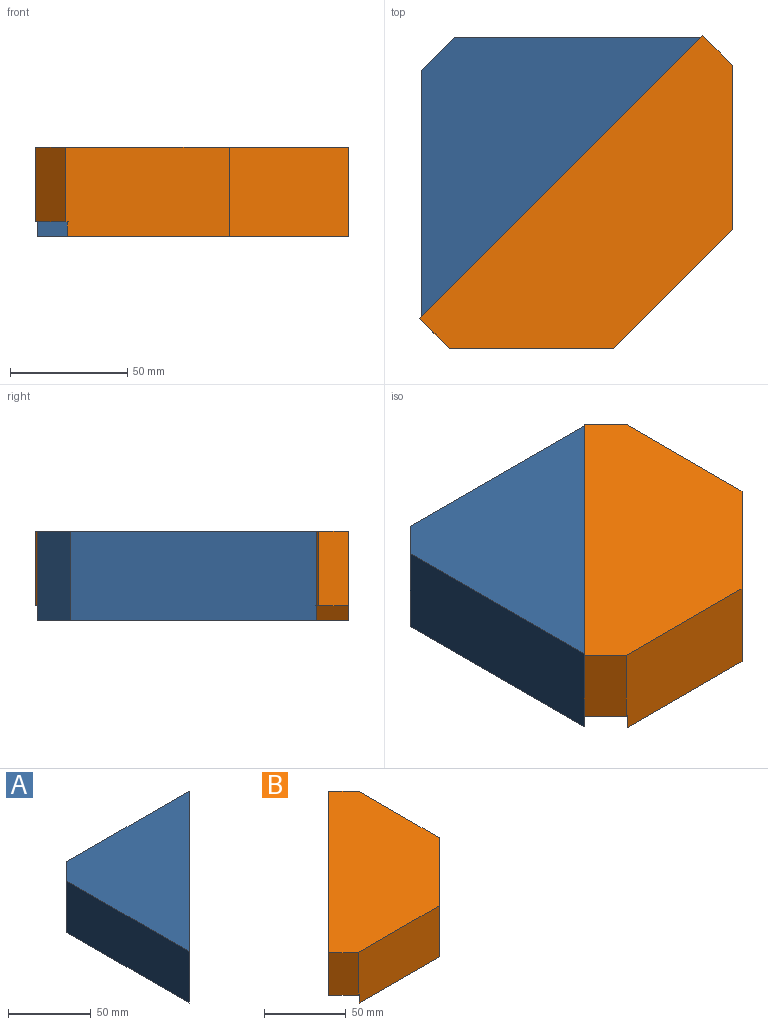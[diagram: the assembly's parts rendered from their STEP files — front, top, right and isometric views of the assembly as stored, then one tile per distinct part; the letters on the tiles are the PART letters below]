
ASSEMBLY  parts=2 mates=1
PART A: 6 faces, bbox 119.1x119.1x38.1 mm
  f0: plane 104.9x38.1mm, normal (0,1,0), area 3996.8mm2, adj f2,f3,f4,f5
  f1: plane 104.9x38.1mm, normal (-1,0,0), area 3996.8mm2, adj f2,f3,f4,f5
  f2: plane 119.13x119.13mm, normal (0,0,1), area 6994.3mm2, adj f0,f1,f4,f5
  f3: plane 119.13x119.13mm, normal (0,0,-1), area 6994.3mm2, adj f0,f1,f4,f5
  f4: plane 38.1x14.22mm, normal (-0.71,0.71,0), area 766.4mm2, adj f0,f1,f2,f3
  f5: plane 119.13x119.13mm, normal (0.71,-0.71,0), area 6418.7mm2, adj f0,f1,f2,f3
PART B: 10 faces, bbox 133.4x133.4x38.1 mm
  f0: plane 133.35x133.35mm, normal (0,0,1), area 9052.4mm2, adj f2,f3,f4,f6,f8,f9
  f1: plane 133.35x133.35mm, normal (0,0,-1), area 3157.2mm2, adj f2,f3,f4,f6,f7,f9
  f2: plane 31.75x12.7mm, normal (0.71,0.71,0), area 570.2mm2, adj f0,f1,f4,f9
  f3: plane 69.85x38.1mm, normal (0,-1,0), area 2656.4mm2, adj f0,f1,f5,f6,f7,f8
  f4: plane 69.85x38.1mm, normal (1,0,0), area 2656.4mm2, adj f0,f1,f2,f5,f7,f8
  f5: plane 119.88x119.88mm, normal (0,0,-1), area 5895.2mm2, adj f3,f4,f7,f8
  f6: plane 31.75x12.7mm, normal (-0.71,-0.71,0), area 570.2mm2, adj f0,f1,f3,f9
  f7: plane 119.88x119.88mm, normal (-0.71,0.71,0), area 1076.5mm2, adj f1,f3,f4,f5
  f8: plane 50.8x50.8mm, normal (0.71,-0.71,0), area 2737.2mm2, adj f0,f3,f4,f5
  f9: plane 120.65x120.65mm, normal (-0.71,0.71,0), area 5417.3mm2, adj f0,f1,f2,f6
PLACE A t=(15.05,-5.54,-38.6)mm
PLACE B t=(14.29,-4.78,-38.6)mm
MATE fastened A.f5 <-> B.f9  axis (0.71,-0.71,0) through (7.94,1.57,-0.5)mm
